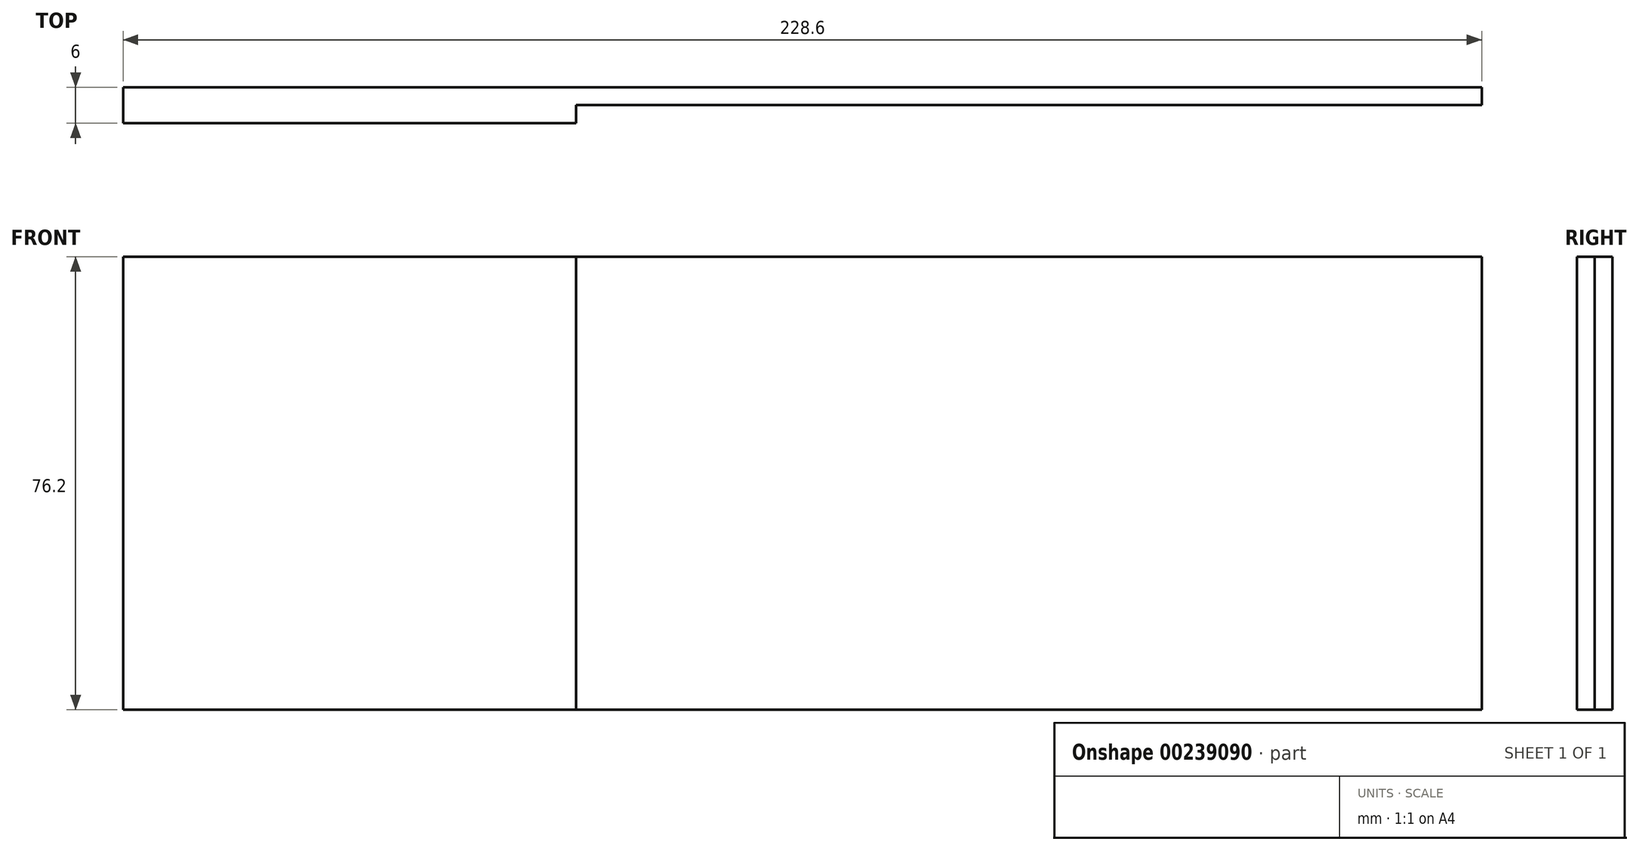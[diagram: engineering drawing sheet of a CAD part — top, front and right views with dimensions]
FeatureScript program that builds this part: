
annotation { "Feature Type Name" : "Feature", "Feature Type Description" : "" }
export const myFeature = defineFeature(function(context is Context, id is Id, definition is map)
    precondition{}
    {
        {
            assignVariable(context, id + "F0", {"name" : "v", "anyValue" : 3});
        }
        {
            var Q0;
            Q0=qCreatedBy(makeId("Front.planeOp"),FACE);
            var sketch = newSketch(context, id + "F1", { "sketchPlane" : qUnion([Q0])});
            skLineSegment(sketch, "E0.bottom", {"start": v(-114.3, 38.1) * mm, "end": v(114.3, 38.1) * mm});
            skLineSegment(sketch, "E0.top", {"start": v(-114.3, -38.1) * mm, "end": v(114.3, -38.1) * mm});
            skLineSegment(sketch, "E0.left", {"start": v(-114.3, 38.1) * mm, "end": v(-114.3, -38.1) * mm});
            skLineSegment(sketch, "E0.right", {"start": v(114.3, 38.1) * mm, "end": v(114.3, -38.1) * mm});
            skPoint(sketch, "E0.middle", {"position": v(0, 0) * mm});
            skSolve(sketch);
        }
        {
            var Q0;
            Q0 = qSketchRegion(id + "F1", true);
            extrude(context, id + "F2", {"entities" : qUnion([Q0]), "depth" : (getVariable(context, 'v')) * mm});
        }
        {
            var Q0;
            Q0=makeQuery(id+"F2.opExtrude","CAP_FACE",FACE,{"disambiguationData":[OSD([sQuery(id+"F1.wireOp",EDGE,"E0.bottom"),sQuery(id+"F1.wireOp",EDGE,"E0.top"),sQuery(id+"F1.wireOp",EDGE,"E0.left"),sQuery(id+"F1.wireOp",EDGE,"E0.right")])],"isStart":false});
            var sketch = newSketch(context, id + "F3", { "sketchPlane" : qUnion([Q0])});
            skLineSegment(sketch, "E1.bottom", {"start": v(-114.3, 38.1) * mm, "end": v(-38.1, 38.1) * mm});
            skLineSegment(sketch, "E1.top", {"start": v(-114.3, -38.1) * mm, "end": v(-38.1, -38.1) * mm});
            skLineSegment(sketch, "E1.left", {"start": v(-114.3, 38.1) * mm, "end": v(-114.3, -38.1) * mm});
            skLineSegment(sketch, "E1.right", {"start": v(-38.1, 38.1) * mm, "end": v(-38.1, -38.1) * mm});
            skSolve(sketch);
        }
        {
            var Q0;
            Q0 = qSketchRegion(id + "F3", true);
            extrude(context, id + "F4", {"entities" : qUnion([Q0]), "operationType" : NewBodyOperationType.ADD, "depth" : (getVariable(context, 'v')) * mm});
        }
    });
